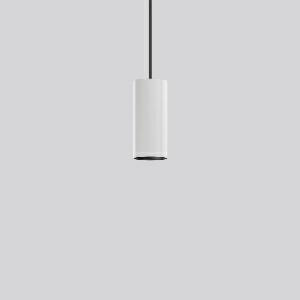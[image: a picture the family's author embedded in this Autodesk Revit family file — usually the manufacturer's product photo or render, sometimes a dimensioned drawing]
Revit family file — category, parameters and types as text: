
# Revit family: deecos_p_mini_911521_002_3_124a
name_source: partatom
category: Lighting Fixtures
units: mm (PartAtom-declared; Revit-internal decimal feet)

## family parameters
Cut with Voids When Loaded = No
Host = Face
Light Source = No
Part Type = Normal
Room Calculation Point = No
Round Connector Dimension = Use Diameter
Shared = No

## types (1)
- DEECOS P mini (1 x LED Modul 935, 3700 lm, 3500)
    Apparent Load = 29 VA
    Approval mark = CE
    CIE Flux Codes = 100 100 100 100 100
    Color Rendering = 92
    Color Temperature = 3500
    Default Elevation = 1800 mm
    Description = Series: DEECOS P mini
Cylindrical pendant luminaire. Housing: die-cast aluminium, powder-coated. Canopy made of powder-coated sheet steel with magnetic attachment. Optical assembly with reflector made of MIRO-Silver with 98% total light reflection for outstanding efficiency - can be changed without tools. Best colour rendering index Ra>90. Transparent pendant cable 5 m, can be shortened, with integrated steel cable. High quality converter without flickering and stroboscopic effect. The following accessories can be mounted without use of tools: interchangeable lenses, honeycomb louvre, clear and frosted diffusers, white interchangeable plastic ring. Decorative recessed suspension set available as accessory.Suitable for accessory Deecos P Tube cylinder extensions 0.5 m, 0.75 m or 1 m. 
Colour: traffic white, matt (RAL 9016)
Diameter: 87 mm
Height: 195 mm
Suspension length: 5000 mm
Lamp: LED
Socket: without socket
Colour temperature: 3500K
Colour rendering index (CRI): 92
System power: 29 W
Rated luminous flux: 3700 lm
Luminous efficiency: 128 lm/W
Control gear: Regulated power supply
Protection class: I
Type of protection: IP 20
    Height = 195 mm
    Lamp = 1 x LED Modul 935
    Lamp Light Flux = 3700 lm
    Lamp count = 1
    Length = 87 mm
    Lifetime = 50000 h
    Luminous efficacy = 128 lm/W
    Manufacturer = RZB
    ModVariant = No
    Model = 911521.002.3
    Mounting Place = Ceiling
    Mounting Type = Pendant
    Number of Poles = 1
    OnlyDefault = Yes
    Power Factor = 1
    Product Name = DEECOS P mini
    Product group = Pendant luminaires
    ProductGroupID = 902
    Protection Class = Protection class I
    Protection Degree = IP 20
    RLX_Detail_Level = 1
    RLX_Emergency_Light_Flux = 0 lm
    RLX_Emergency_Type = 0
    RLX_Emergency_Type_DB = No
    RlxData = <blob elided: 55041 chars, md5=a3bed2d9>
    Socket = socket
    Standby Power = 0 W
    System Light Flux = 3700 lm
    System Power = 29 W
    Type Comments = Product without accessories
    Type Image = 911476.002.jpg
    URL = http://relux.com
    VarID = ---
    Voltage = 230 V
    Voltage Range = 220-240 V
    Weight = 0.00 kg
    Width = 0 mm  [stored 0 ft]

note: [stored X ft] marks values corroborated as IEEE doubles in the binary element streams (Revit-internal decimal feet)

## geometry (parser evidence)
native form markers: Blend x4, Sweep x12
no freeform markers — native parametric forms only
